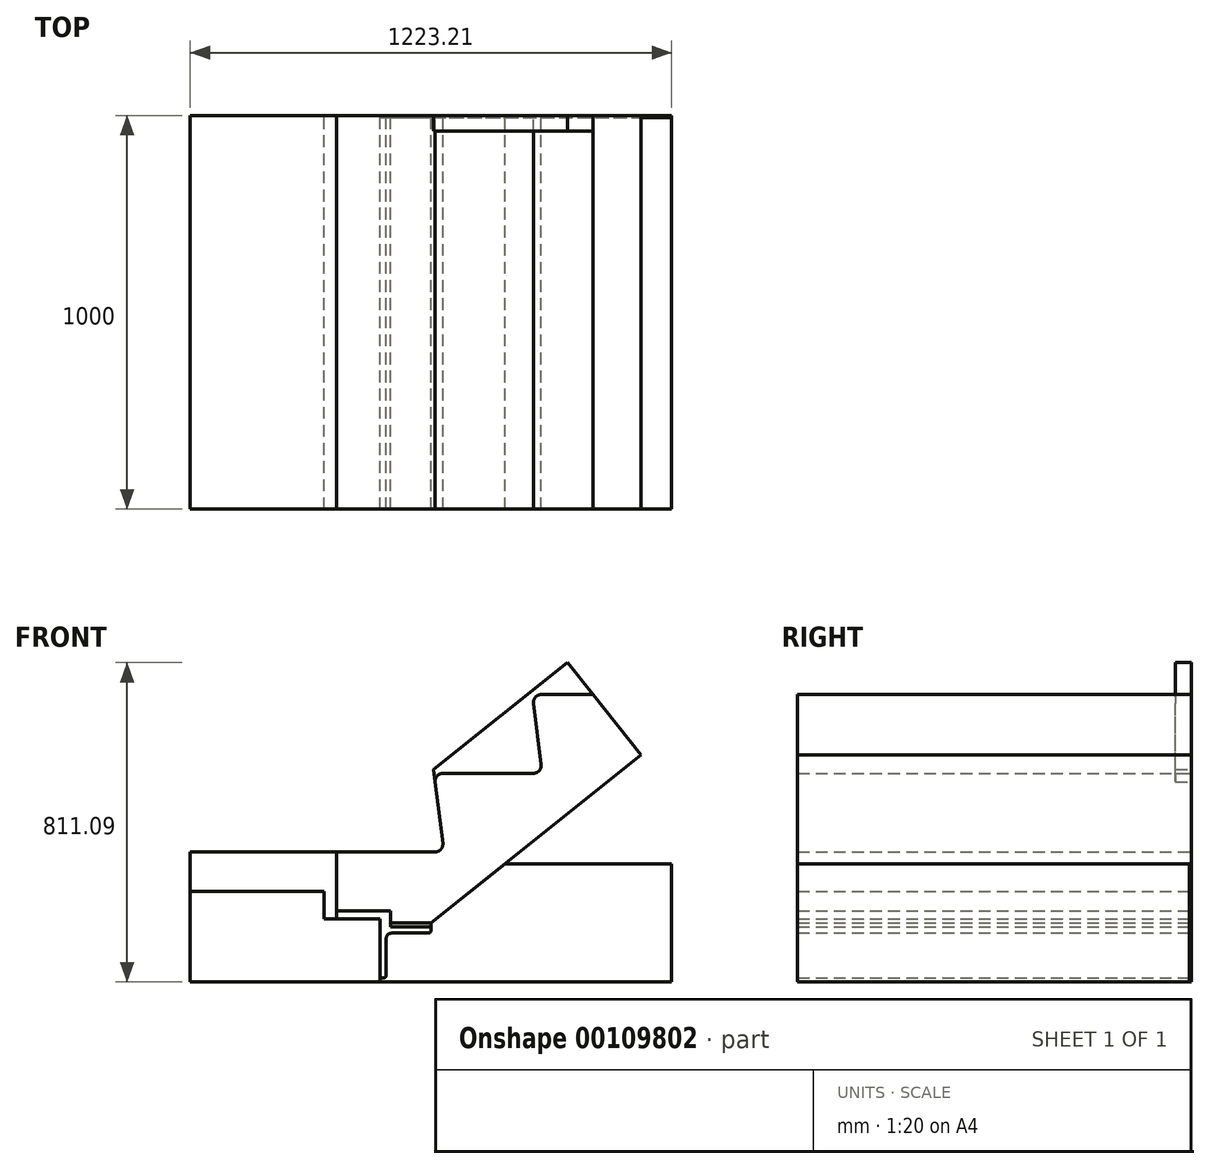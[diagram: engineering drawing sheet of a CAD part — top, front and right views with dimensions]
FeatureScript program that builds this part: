
annotation { "Feature Type Name" : "Feature", "Feature Type Description" : "" }
export const myFeature = defineFeature(function(context is Context, id is Id, definition is map)
    precondition{}
    {
        {
            var Q0;
            Q0=qCreatedBy(makeId("Front.planeOp"),FACE);
            var sketch = newSketch(context, id + "F0", { "sketchPlane" : qUnion([Q0])});
            skLineSegment(sketch, "E0", {"start": v(-258.27, -19.33) * mm, "end": v(-8.74, -19.33) * mm});
            skLineSegment(sketch, "E1", {"start": v(11.1, 3.15) * mm, "end": v(-12.25, 190) * mm});
            skLineSegment(sketch, "E2", {"start": v(-12.25, 190) * mm, "end": v(327.44, 461.76) * mm});
            skLineSegment(sketch, "E3", {"start": v(-148.68, -349.33) * mm, "end": v(-630.63, -349.33) * mm});
            skLineSegment(sketch, "E4", {"start": v(-18.68, -199.33) * mm, "end": v(-121.84, -199.33) * mm});
            skLineSegment(sketch, "E5", {"start": v(11.58, 180.67) * mm, "end": v(241.26, 180.67) * mm});
            skLineSegment(sketch, "E6", {"start": v(261.1, 203.15) * mm, "end": v(241.73, 358.2) * mm});
            skLineSegment(sketch, "E7", {"start": v(261.58, 380.67) * mm, "end": v(392.26, 380.67) * mm});
            skLineSegment(sketch, "E8", {"start": v(-148.68, -189.33) * mm, "end": v(-148.68, -349.33) * mm});
            skLineSegment(sketch, "E9", {"start": v(-290, -189.33) * mm, "end": v(-290, -119.33) * mm});
            skLineSegment(sketch, "E10", {"start": v(-121.84, -169.33) * mm, "end": v(-258.27, -169.33) * mm});
            skLineSegment(sketch, "E11", {"start": v(-148.68, -189.33) * mm, "end": v(-290, -189.33) * mm});
            skLineSegment(sketch, "E12", {"start": v(-258.27, -169.33) * mm, "end": v(-258.27, -19.33) * mm});
            skLineSegment(sketch, "E13", {"start": v(260.59, 545.38) * mm, "end": v(630.63, 82.5) * mm});
            skLineSegment(sketch, "E14", {"start": v(-630.63, 87.12) * mm, "end": v(-630.63, -443.05) * mm});
            skArc(sketch, "E15", {"start": v(-8.74, -19.33) * mm, "mid": v(6.26, -12.56) * mm, "end": v(11.1, 3.15) * mm});
            skArc(sketch, "E16", {"start": v(11.58, 180.67) * mm, "mid": v(-3.42, 173.9) * mm, "end": v(-8.27, 158.2) * mm});
            skArc(sketch, "E17", {"start": v(241.26, 180.67) * mm, "mid": v(256.26, 187.44) * mm, "end": v(261.1, 203.15) * mm});
            skArc(sketch, "E18", {"start": v(261.58, 380.67) * mm, "mid": v(246.58, 373.9) * mm, "end": v(241.73, 358.2) * mm});
            skLineSegment(sketch, "E19", {"start": v(-148.68, -349.33) * mm, "end": v(592.58, -349.33) * mm});
            skLineSegment(sketch, "E20", {"start": v(168.82, -49.33) * mm, "end": v(592.58, -49.33) * mm});
            skLineSegment(sketch, "E21", {"start": v(592.58, 18.95) * mm, "end": v(592.58, -393.06) * mm});
            skLineSegment(sketch, "E22", {"start": v(-18.68, -199.33) * mm, "end": v(514.77, 227.43) * mm});
            skLineSegment(sketch, "E23", {"start": v(-148.68, -299.33) * mm, "end": v(-630.63, -299.33) * mm});
            skLineSegment(sketch, "E24", {"start": v(-121.84, -199.33) * mm, "end": v(-121.84, -169.33) * mm});
            skLineSegment(sketch, "E25", {"start": v(-290, -119.33) * mm, "end": v(-630.63, -119.33) * mm});
            skLineSegment(sketch, "E26", {"start": v(-258.27, -19.33) * mm, "end": v(-630.63, -19.33) * mm});
            skLineSegment(sketch, "E27", {"start": v(-258.27, -169.33) * mm, "end": v(-258.27, -189.33) * mm});
            skLineSegment(sketch, "E28", {"start": v(-148.68, -189.33) * mm, "end": v(-148.68, -169.33) * mm});
            skLineSegment(sketch, "E29", {"start": v(-258.27, -169.33) * mm, "end": v(-148.68, -189.33) * mm});
            skLineSegment(sketch, "E30", {"start": v(-148.68, -169.33) * mm, "end": v(-258.27, -189.33) * mm});
            skArc(sketch, "E31", {"start": v(-132.68, -239.33) * mm, "mid": v(-128.58, -229.43) * mm, "end": v(-118.68, -225.33) * mm});
            skLineSegment(sketch, "E32", {"start": v(-118.68, -225.33) * mm, "end": v(-25.68, -225.33) * mm});
            skArc(sketch, "E33", {"start": v(-25.68, -225.33) * mm, "mid": v(-20.73, -223.28) * mm, "end": v(-18.68, -218.33) * mm});
            skLineSegment(sketch, "E34", {"start": v(-18.68, -218.33) * mm, "end": v(-18.68, -209.33) * mm});
            skLineSegment(sketch, "E35", {"start": v(-18.68, -209.33) * mm, "end": v(-148.68, -209.33) * mm});
            skLineSegment(sketch, "E36", {"start": v(-148.68, -209.33) * mm, "end": v(-148.68, -339.33) * mm});
            skLineSegment(sketch, "E37", {"start": v(-148.68, -339.33) * mm, "end": v(-139.68, -339.33) * mm});
            skArc(sketch, "E38", {"start": v(-139.68, -339.33) * mm, "mid": v(-134.73, -337.28) * mm, "end": v(-132.68, -332.33) * mm});
            skLineSegment(sketch, "E39", {"start": v(-132.68, -332.33) * mm, "end": v(-132.68, -239.33) * mm});
            skLineSegment(sketch, "E40", {"start": v(122.07, -484.72) * mm, "end": v(142.07, -484.72) * mm});
            skLineSegment(sketch, "E41", {"start": v(142.07, -484.72) * mm, "end": v(142.07, -524.72) * mm});
            skLineSegment(sketch, "E42", {"start": v(142.07, -524.72) * mm, "end": v(122.07, -524.72) * mm});
            skLineSegment(sketch, "E43", {"start": v(122.07, -524.72) * mm, "end": v(122.07, -484.72) * mm});
            skLineSegment(sketch, "E44", {"start": v(122.07, -494.72) * mm, "end": v(142.07, -494.72) * mm});
            skLineSegment(sketch, "E45", {"start": v(122.07, -514.72) * mm, "end": v(142.07, -514.72) * mm});
            skEllipse(sketch, "E46", {"center": v(132.07, -489.72) * mm, "majorRadius": 10 * mm, "minorRadius": 5 * mm, "majorAxis": v(-1, 0)});
            skEllipse(sketch, "E47", {"center": v(132.07, -519.72) * mm, "majorRadius": 10 * mm, "minorRadius": 5 * mm, "majorAxis": v(-1, 0)});
            skEllipse(sketch, "E48", {"center": v(132.07, -504.72) * mm, "majorRadius": 10 * mm, "minorRadius": 10 * mm, "majorAxis": v(0, 1)});
            skLineSegment(sketch, "E49", {"start": v(142.07, -497.72) * mm, "end": v(148.92, -497.72) * mm});
            skLineSegment(sketch, "E50", {"start": v(142.07, -511.72) * mm, "end": v(148.92, -511.72) * mm});
            skLineSegment(sketch, "E51", {"start": v(148.92, -497.72) * mm, "end": v(148.92, -511.72) * mm});
            skLineSegment(sketch, "E52", {"start": v(117.07, -529.72) * mm, "end": v(122.07, -529.72) * mm});
            skLineSegment(sketch, "E53", {"start": v(122.07, -529.72) * mm, "end": v(122.07, -479.72) * mm});
            skLineSegment(sketch, "E54", {"start": v(122.07, -479.72) * mm, "end": v(117.07, -479.72) * mm});
            skLineSegment(sketch, "E55", {"start": v(117.07, -479.72) * mm, "end": v(117.07, -529.72) * mm});
            skCircle(sketch, "E56", {"center": v(246.23, -520.38) * mm, "radius": 7 * mm});
            skLineSegment(sketch, "E57", {"start": v(228.91, -510.38) * mm, "end": v(228.91, -530.38) * mm});
            skLineSegment(sketch, "E58", {"start": v(263.56, -510.38) * mm, "end": v(263.56, -530.38) * mm});
            skLineSegment(sketch, "E59", {"start": v(228.91, -510.38) * mm, "end": v(246.23, -500.38) * mm});
            skLineSegment(sketch, "E60", {"start": v(246.23, -500.38) * mm, "end": v(263.56, -510.38) * mm});
            skLineSegment(sketch, "E61", {"start": v(228.91, -530.38) * mm, "end": v(246.23, -540.38) * mm});
            skLineSegment(sketch, "E62", {"start": v(246.23, -540.38) * mm, "end": v(263.56, -530.38) * mm});
            skCircle(sketch, "E63", {"center": v(246.23, -520.38) * mm, "radius": 25 * mm});
            skLineSegment(sketch, "E64", {"start": v(-121.84, -199.33) * mm, "end": v(-121.84, -209.33) * mm});
            skLineSegment(sketch, "E65", {"start": v(-18.68, -199.33) * mm, "end": v(-18.68, -209.33) * mm});
            skSolve(sketch);
        }
        {
            var Q0;
            {var subQ1=sQuery(id+"F0.wireOp",EDGE,"E9");Q0=makeQuery(id+"F0.imprint","IMPRINT",FACE,{"disambiguationData":[TD([[makeQuery(id+"F0.imprint","IMPRINT",EDGE,{"derivedFrom":subQ1}),1.0]])]});}
            var Q1;
            {var subQ2=sQuery(id+"F0.wireOp",EDGE,"E3");Q1=makeQuery(id+"F0.imprint","IMPRINT",FACE,{"disambiguationData":[TD([[makeQuery(id+"F0.imprint","IMPRINT",EDGE,{"derivedFrom":subQ2}),-1.0]])]});}
            extrude(context, id + "F1", {"entities" : qUnion([Q0, Q1]), "depth" : 1000 * mm});
        }
        {
            var Q0;
            {var subQ4=sQuery(id+"F0.wireOp",EDGE,"E9");Q0=makeQuery(id+"F0.imprint","IMPRINT",FACE,{"disambiguationData":[TD([[makeQuery(id+"F0.imprint","IMPRINT",EDGE,{"derivedFrom":subQ4}),-1.0]])]});}
            extrude(context, id + "F2", {"entities" : qUnion([Q0]), "depth" : 1000 * mm});
        }
        {
            var Q0;
            Q0=makeQuery(id+"F0.imprint","IMPRINT",FACE,{"disambiguationData":[TD([[makeQuery(id+"F0.imprint","IMPRINT",EDGE,{"derivedFrom":sQuery(id+"F0.wireOp",EDGE,"E0")}),-1.0]])]});
            extrude(context, id + "F3", {"entities" : qUnion([Q0]), "depth" : 1000 * mm});
        }
        {
            var Q0;
            {var subQ1=sQuery(id+"F0.wireOp",EDGE,"E2");Q0=makeQuery(id+"F0.imprint","IMPRINT",FACE,{"disambiguationData":[TD([[makeQuery(id+"F0.imprint","IMPRINT",EDGE,{"derivedFrom":subQ1}),-1.0]])]});}
            extrude(context, id + "F4", {"entities" : qUnion([Q0]), "depth" : 40 * mm});
        }
        {
            var Q0;
            Q0=makeQuery(id+"F0.imprint","IMPRINT",FACE,{"disambiguationData":[TD([[makeQuery(id+"F0.imprint","IMPRINT",EDGE,{"derivedFrom":sQuery(id+"F0.wireOp",EDGE,"E31")}),1.0]])]});
            extrude(context, id + "F5", {"entities" : qUnion([Q0]), "depth" : 1000 * mm});
        }
        {
            var Q0;
            Q0=makeQuery(id+"F0.imprint","IMPRINT",FACE,{"disambiguationData":[TD([[makeQuery(id+"F0.imprint","IMPRINT",EDGE,{"derivedFrom":sQuery(id+"F0.wireOp",EDGE,"E4")}),1.0]])]});
            extrude(context, id + "F6", {"entities" : qUnion([Q0]), "depth" : 1000 * mm});
        }
        {
            var Q0;
            {var subQ0=sQuery(id+"F0.wireOp",EDGE,"E19");Q0=makeQuery(id+"F0.imprint","IMPRINT",FACE,{"disambiguationData":[TD([[makeQuery(id+"F0.imprint","IMPRINT",EDGE,{"derivedFrom":subQ0}),1.0]])]});}
            extrude(context, id + "F7", {"entities" : qUnion([Q0]), "depth" : 5 * mm});
        }
    });
